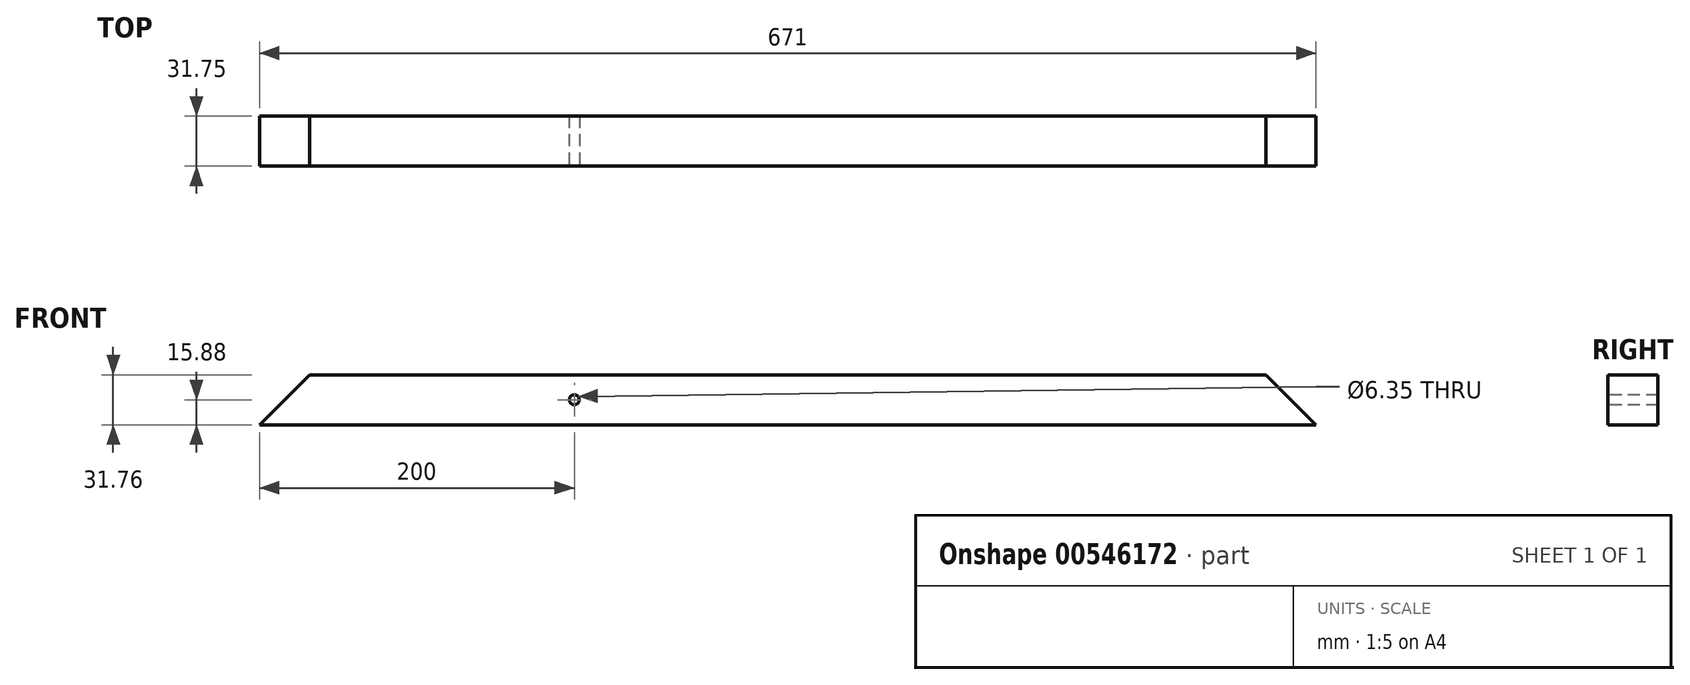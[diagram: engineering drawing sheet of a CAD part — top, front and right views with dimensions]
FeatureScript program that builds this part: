
annotation { "Feature Type Name" : "Feature", "Feature Type Description" : "" }
export const myFeature = defineFeature(function(context is Context, id is Id, definition is map)
    precondition{}
    {
        {
            var Q0;
            Q0=qCreatedBy(makeId("Front.planeOp"),FACE);
            var sketch = newSketch(context, id + "F0", { "sketchPlane" : qUnion([Q0])});
            skLineSegment(sketch, "E0.bottom", {"start": v(335.5, 15.88) * mm, "end": v(-335.5, 15.88) * mm});
            skLineSegment(sketch, "E0.top", {"start": v(335.5, -15.88) * mm, "end": v(-335.5, -15.88) * mm});
            skLineSegment(sketch, "E0.left", {"start": v(335.5, 15.88) * mm, "end": v(335.5, -15.88) * mm});
            skLineSegment(sketch, "E0.right", {"start": v(-335.5, 15.88) * mm, "end": v(-335.5, -15.88) * mm});
            skPoint(sketch, "E0.middle", {"position": v(0, 0) * mm});
            skSolve(sketch);
        }
        {
            var Q0;
            Q0=makeQuery(id+"F0.imprint","IMPRINT",FACE,{"disambiguationData":[TD([[makeQuery(id+"F0.imprint","IMPRINT",EDGE,{"derivedFrom":sQuery(id+"F0.wireOp",EDGE,"E0.bottom")}),1.0]])]});
            extrude(context, id + "F1", {"entities" : qUnion([Q0]), "depth" : 31.75 * mm, "offsetDistance" : 25.4 * mm});
        }
        {
            var Q0;
            Q0=makeQuery(id+"F1.opExtrude","CAP_FACE",FACE,{"disambiguationData":[OSD([sQuery(id+"F0.wireOp",EDGE,"E0.bottom"),sQuery(id+"F0.wireOp",EDGE,"E0.top"),sQuery(id+"F0.wireOp",EDGE,"E0.left"),sQuery(id+"F0.wireOp",EDGE,"E0.right")])],"isStart":false});
            var sketch = newSketch(context, id + "F2", { "sketchPlane" : qUnion([Q0])});
            skLineSegment(sketch, "E1", {"start": v(-335.5, -15.88) * mm, "end": v(-303.75, 15.87) * mm});
            skLineSegment(sketch, "E2", {"start": v(335.5, -15.88) * mm, "end": v(303.75, 15.88) * mm});
            skSolve(sketch);
        }
        {
            var Q0;
            {var subQ0=sQuery(id+"F2.wireOp",EDGE,"E1");Q0=makeQuery(id+"F2.imprint","IMPRINT",FACE,{"disambiguationData":[TD([[makeQuery(id+"F2.imprint","IMPRINT",EDGE,{"derivedFrom":subQ0}),1.0]])]});}
            var Q1;
            {var subQ0=sQuery(id+"F2.wireOp",EDGE,"E2");Q1=makeQuery(id+"F2.imprint","IMPRINT",FACE,{"disambiguationData":[TD([[makeQuery(id+"F2.imprint","IMPRINT",EDGE,{"derivedFrom":subQ0}),-1.0]])]});}
            extrude(context, id + "F3", {"entities" : qUnion([Q0, Q1]), "operationType" : NewBodyOperationType.REMOVE, "endBound" : BoundingType.THROUGH_ALL, "oppositeDirection" : true, "depth" : 25.4 * mm, "offsetDistance" : 25.4 * mm});
        }
        {
            var Q0;
            Q0=makeQuery(id+"F1.opExtrude","CAP_FACE",FACE,{"disambiguationData":[OSD([sQuery(id+"F0.wireOp",EDGE,"E0.bottom"),sQuery(id+"F0.wireOp",EDGE,"E0.top"),sQuery(id+"F0.wireOp",EDGE,"E0.left"),sQuery(id+"F0.wireOp",EDGE,"E0.right")])],"isStart":false});
            var sketch = newSketch(context, id + "F4", { "sketchPlane" : qUnion([Q0])});
            skCircle(sketch, "E3", {"center": v(-135.5, 0) * mm, "radius": 3.18 * mm});
            skPoint(sketch, "E3.centerSnap0", {"position": v(-319.62, 0) * mm});
            skLineSegment(sketch, "E4", {"start": v(-335.5, -15.88) * mm, "end": v(-135.5, -15.88) * mm});
            skSolve(sketch);
        }
        {
            var Q0;
            Q0=makeQuery(id+"F4.imprint","IMPRINT",FACE,{"disambiguationData":[TD([[makeQuery(id+"F4.imprint","IMPRINT",EDGE,{"derivedFrom":sQuery(id+"F4.wireOp",EDGE,"E3")}),1.0]])]});
            extrude(context, id + "F5", {"entities" : qUnion([Q0]), "operationType" : NewBodyOperationType.REMOVE, "endBound" : BoundingType.THROUGH_ALL, "oppositeDirection" : true, "depth" : 25.4 * mm, "offsetDistance" : 25.4 * mm});
        }
    });
